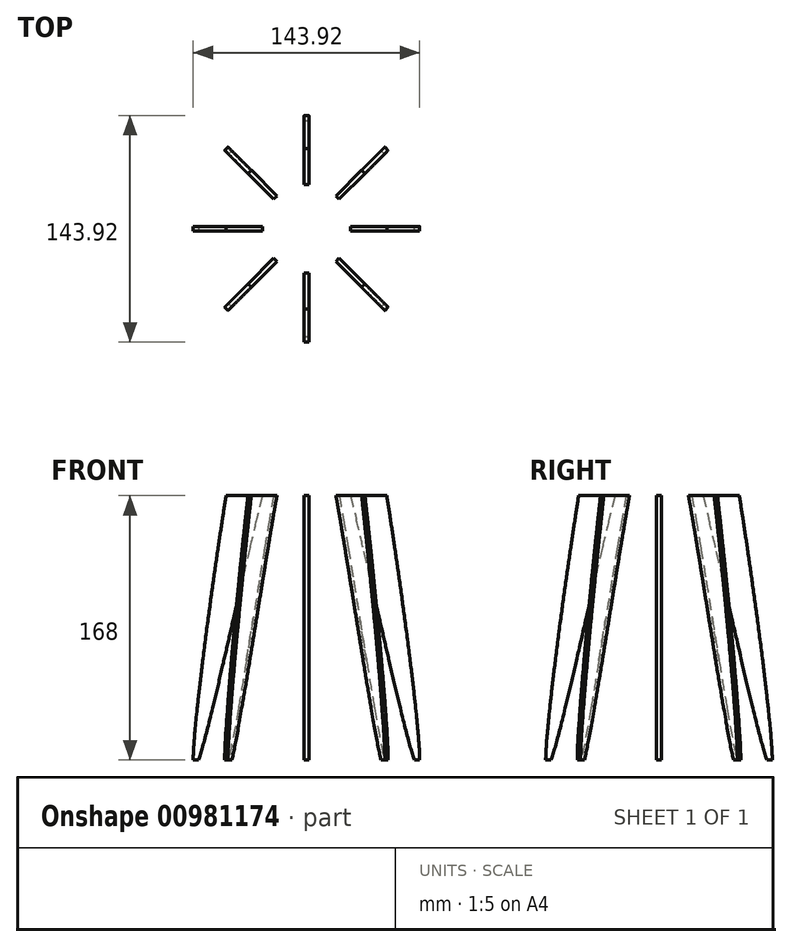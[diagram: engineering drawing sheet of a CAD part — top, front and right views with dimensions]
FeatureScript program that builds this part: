
annotation { "Feature Type Name" : "Feature", "Feature Type Description" : "" }
export const myFeature = defineFeature(function(context is Context, id is Id, definition is map)
    precondition{}
    {
        {
            var Q0;
            Q0=qCreatedBy(makeId("Front.planeOp"),FACE);
            var sketch = newSketch(context, id + "F0", { "sketchPlane" : qUnion([Q0])});
            skFitSpline(sketch, "E0", {"points": [v(0, 0) * mm, v(21.74, 85.26) * mm, v(71.9, -106.65) * mm, v(20.47, 170) * mm, v(0, 170) * mm], "startDerivative": vector(299.16, 623.39) * mm, "endDerivative": vector(-645.11, 2521.01) * mm});
            skFitSpline(sketch, "E1.MirrorCS", {"points": [v(0, 0) * mm, v(-21.74, 85.26) * mm, v(-71.9, -106.65) * mm, v(-20.47, 170) * mm, v(0, 170) * mm], "startDerivative": vector(-299.16, 623.39) * mm, "endDerivative": vector(645.11, 2521.01) * mm});
            skLineSegment(sketch, "E2", {"start": v(-51.03, 63.9) * mm, "end": v(51.03, 63.9) * mm});
            skLineSegment(sketch, "E3", {"start": v(-53.35, 48.9) * mm, "end": v(53.35, 48.9) * mm});
            skLineSegment(sketch, "E4", {"start": v(-56.05, 30.9) * mm, "end": v(56.05, 30.9) * mm});
            skLineSegment(sketch, "E5", {"start": v(-59.08, 9.9) * mm, "end": v(59.08, 9.9) * mm});
            skLineSegment(sketch, "E6", {"start": v(-62.39, -14.1) * mm, "end": v(62.39, -14.1) * mm});
            skLineSegment(sketch, "E7", {"start": v(-65.88, -41.1) * mm, "end": v(65.88, -41.1) * mm});
            skLineSegment(sketch, "E8", {"start": v(-69.37, -71.1) * mm, "end": v(69.37, -71.1) * mm});
            skLineSegment(sketch, "E9", {"start": v(-71.96, -104.1) * mm, "end": v(71.96, -104.1) * mm});
            skSolve(sketch);
        }
        {
            var Q0;
            Q0=makeQuery(id+"F0.imprint","IMPRINT",FACE,{"disambiguationData":[TD([[makeQuery(id+"F0.imprint","IMPRINT",EDGE,{"derivedFrom":sQuery(id+"F0.wireOp",EDGE,"E0")}),1.0]])]});
            extrude(context, id + "F1", {"entities" : qUnion([Q0]), "depth" : 3 * mm, "offsetDistance" : 25 * mm});
        }
        {
            var Q0;
            Q0=qCreatedBy(makeId("Top.planeOp"),FACE);
            var sketch = newSketch(context, id + "F2", { "sketchPlane" : qUnion([Q0])});
            skPoint(sketch, "E10.0", {"position": v(0, -1.5) * mm});
            skCircle(sketch, "E11", {"center": v(0, -1.5) * mm, "radius": 15 * mm, "construction": true});
            skSolve(sketch);
        }
        {
            var Q0;
            Q0=makeQuery(id+"F1.opExtrude","SWEPT_BODY",BODY,{"disambiguationData":[OSD([sQuery(id+"F0.wireOp",EDGE,"E0"),sQuery(id+"F0.wireOp",EDGE,"E1.MirrorCS")])]});
            var Q1;
            Q1=sQuery(id+"F2.wireOp",EDGE,"E11");
            circularPattern(context, id + "F3", {"entities" : qUnion([Q0]), "axis" : qUnion([Q1]), "angle" : 360 * degree, "instanceCount" : 8, "equalSpace" : true});
        }
    });
